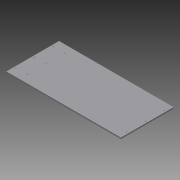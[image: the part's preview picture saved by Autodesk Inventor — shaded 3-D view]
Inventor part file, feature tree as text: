
AUTODESK INVENTOR PART (.ipt)
format: ipt  version: 2015 (Build 190159000, 159)  size: 101,888 bytes
history: native  units: mm
features: reference x4, sketch x2, extrude x1, hole x1
ambient origin geometry x8: Origin, YZ Plane, XZ Plane, XY Plane, X Axis, Y Axis, Z Axis, Center Point
bodies: Solid1 (feature_tree)
feature tree (8):
  extrude  "Extrusion1"  Depth=6.35mm
  hole  "Hole1"  [1 undecoded]
  sketch  "Sketch1"  dims[d0=6.35mm d1=0.0mm d2=20.0mm]
  reference  "Reference1"
  reference  "Reference2"
  reference  "Reference3"
  reference  "Reference4"
  sketch  "Sketch2"  dims[d3=80.0mm d4=80.0mm d5=20.0mm d6=140.0mm d7=4.5mm d8=6.0mm d9=8.0mm d10=4.0mm d11=90.0deg d12=8.0mm d13=20.594885mm]
note: 1 required parameter value undecoded (feature->parameter linkage not recoverable at this tier; creation-order binding heuristic only, values carry confidence <= 0.55)
